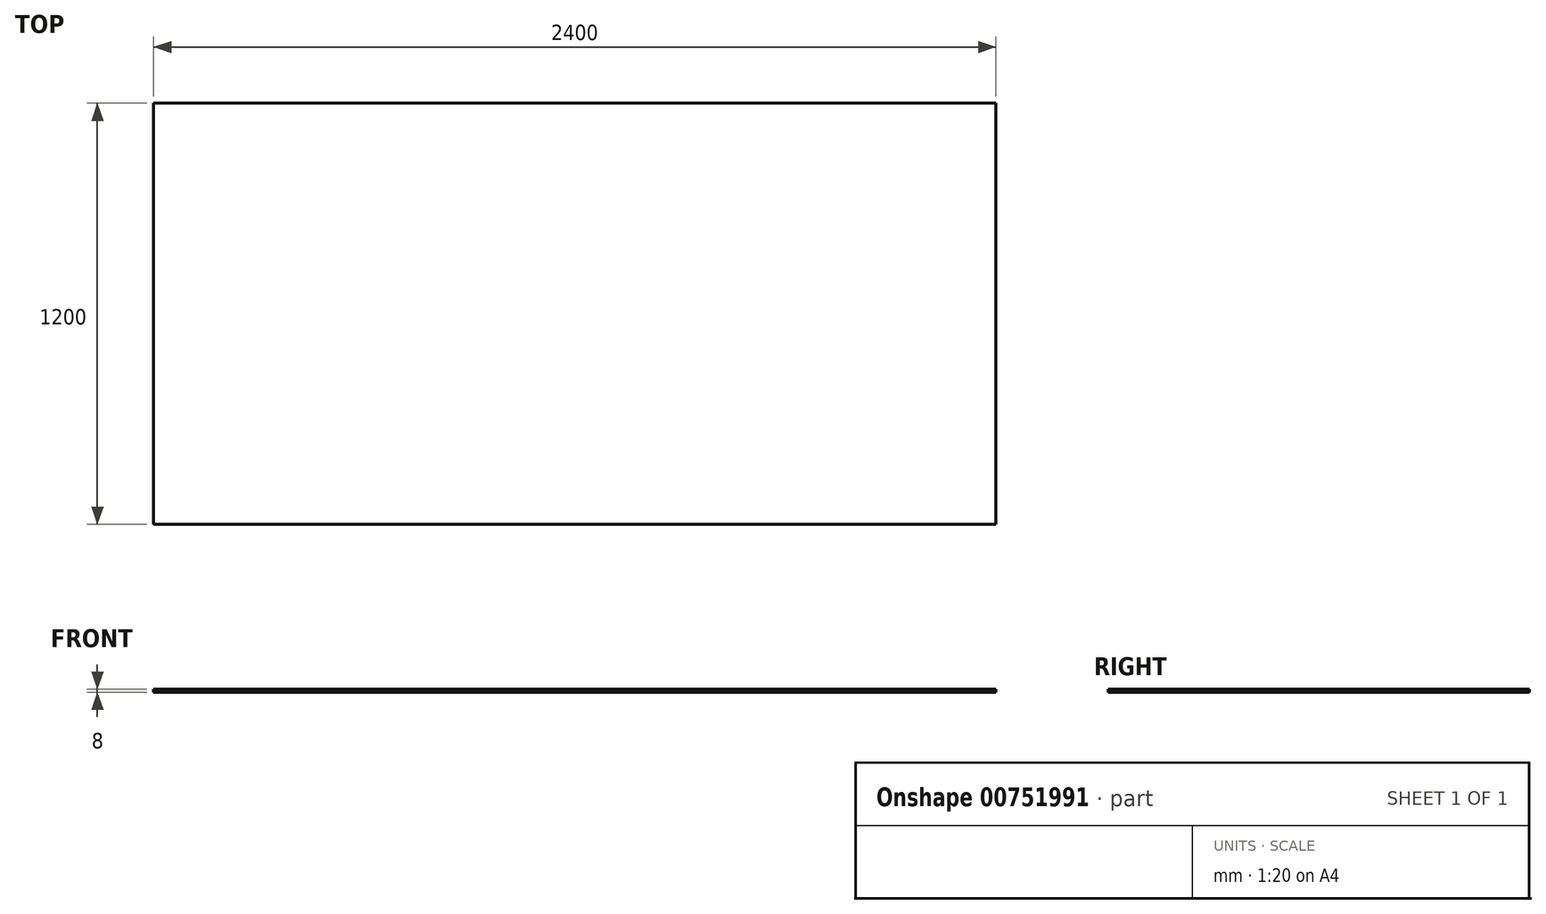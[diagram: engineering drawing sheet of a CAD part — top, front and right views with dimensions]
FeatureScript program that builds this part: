
annotation { "Feature Type Name" : "Feature", "Feature Type Description" : "" }
export const myFeature = defineFeature(function(context is Context, id is Id, definition is map)
    precondition{}
    {
        {
            var Q0;
            Q0=qCreatedBy(makeId("Top.planeOp"),FACE);
            var sketch = newSketch(context, id + "F0", { "sketchPlane" : qUnion([Q0])});
            skLineSegment(sketch, "E0.bottom", {"start": v(-2216.95, 1114.89) * mm, "end": v(183.05, 1114.89) * mm});
            skLineSegment(sketch, "E0.top", {"start": v(-2216.95, -85.11) * mm, "end": v(183.05, -85.11) * mm});
            skLineSegment(sketch, "E0.left", {"start": v(-2216.95, 1114.89) * mm, "end": v(-2216.95, -85.11) * mm});
            skLineSegment(sketch, "E0.right", {"start": v(183.05, 1114.89) * mm, "end": v(183.05, -85.11) * mm});
            skSolve(sketch);
        }
        {
            var Q0;
            Q0 = qSketchRegion(id + "F0", true);
            extrude(context, id + "F1", {"entities" : qUnion([Q0]), "depth" : 8 * mm, "offsetDistance" : 25 * mm});
        }
    });
